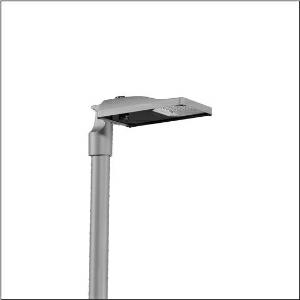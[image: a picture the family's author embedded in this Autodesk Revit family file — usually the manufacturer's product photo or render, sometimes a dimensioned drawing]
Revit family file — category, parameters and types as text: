
# Revit family: streetlight_sl_31_micro___pl52_5xh5h31t08da_3d46
name_source: partatom
category: Lighting Fixtures
units: mm (PartAtom-declared; Revit-internal decimal feet)

## family parameters
Cut with Voids When Loaded = No
Host = Face
Light Source = No
Part Type = Normal
Room Calculation Point = No
Round Connector Dimension = Use Diameter
Shared = No

## types (1)
- --- (1 x LED, 4850 lm, 37.7 W, 3000K)
    Apparent Load = 38 VA
    CIE Flux Codes = 27 59 98 100 100
    Color Rendering = 70
    Color Temperature = 3000K
    Default Elevation = 1800 mm
    Description = Streetlight SL 31 micro D4i, Desk-Remote mast luminaire for post-top, side-entry; light control with lens of PMMA; light distribution: PL52, direct asymmetric distribution, for standard-compliant lighting for roads and squares; LED: luminous flux: 4.850lm, light colour: 730, colour temperature: 3000K; luminous efficacy: 128,6lm/W; control: pre-setting: logarithmic dimming characteristic, flexible luminous flux parameterisation, time-dependent luminous flux control, constant luminous flux control, power reduction, intelligent temperature release in ECG and LED module, overheat protection; luminaire housing, of diecast aluminium, SITECO metallic grey (DB 702S), corrosivity category C5 high according to DIN EN ISO 12944; cover of toughened safety glass, transparent, opened without tools; mast flange of diecast aluminium, SITECO metallic grey (DB 702S), spigot size: 76/60mm, mast flange included unmounted; with cable H07RN-F 2x 1.5mm², cable length: 6,5m, connection cable pre-assembled; mains connection: 220..240V, AC, 50/60Hz; power consumption (at start of service life): 37,7W / (at end of service life): 40,9W / (with reduced operation 50%): 16,3W; protection rating (complete): IP66; insulation class (complete): insulation class II (safety insulation); impact resistance: IK09; certification: CE, ENEC, ENEC+, VDE, UKCA, ZD4i; permissible operating ambient temperature for outdoor applications: -40..+50°C; packaging unit: 1 piece

Light Distribution: PL52
    Height = 76 mm
    Lamp = 1 x LED
    Lamp Light Flux = 4850 lm
    Lamp Power = 37.7 W
    Lamp count = 1
    Length = 467 mm
    Luminous efficacy = 129 lm/W
    Manufacturer = Siteco
    ModVariant = No
    Model = 5XH5H31T08DA
    Number of Poles = 1
    OnlyDefault = Yes
    Power Factor = 1
    Product Name = Streetlight SL 31 micro | PL52
    Product group = mast luminaire | pylon top
    ProductGroupID = 6100
    Protection Class = Protection class II
    Protection Degree = IP 66
    RLX_Detail_Level = 1
    RLX_Emergency_Light_Flux = 0 lm
    RLX_Emergency_Type = 0
    RLX_Emergency_Type_DB = No
    RlxData = <blob elided: 53953 chars, md5=2bb7e2ef>
    Socket = socket
    Standby Power = 0 W
    System Light Flux = 4850 lm
    System Power = 38 W
    Type Comments = factory setting: luminous flux: 100 % | dim-lin: 254 | 745 mA
    Type Image = l_1300315.jpg
    URL = http://relux.com
    VarID = @adj_055503
    Voltage = 0 V
    Weight = 0.00 kg
    Width = 265 mm

## geometry (parser evidence)
native form markers: Blend x4, Sweep x10
no freeform markers — native parametric forms only
